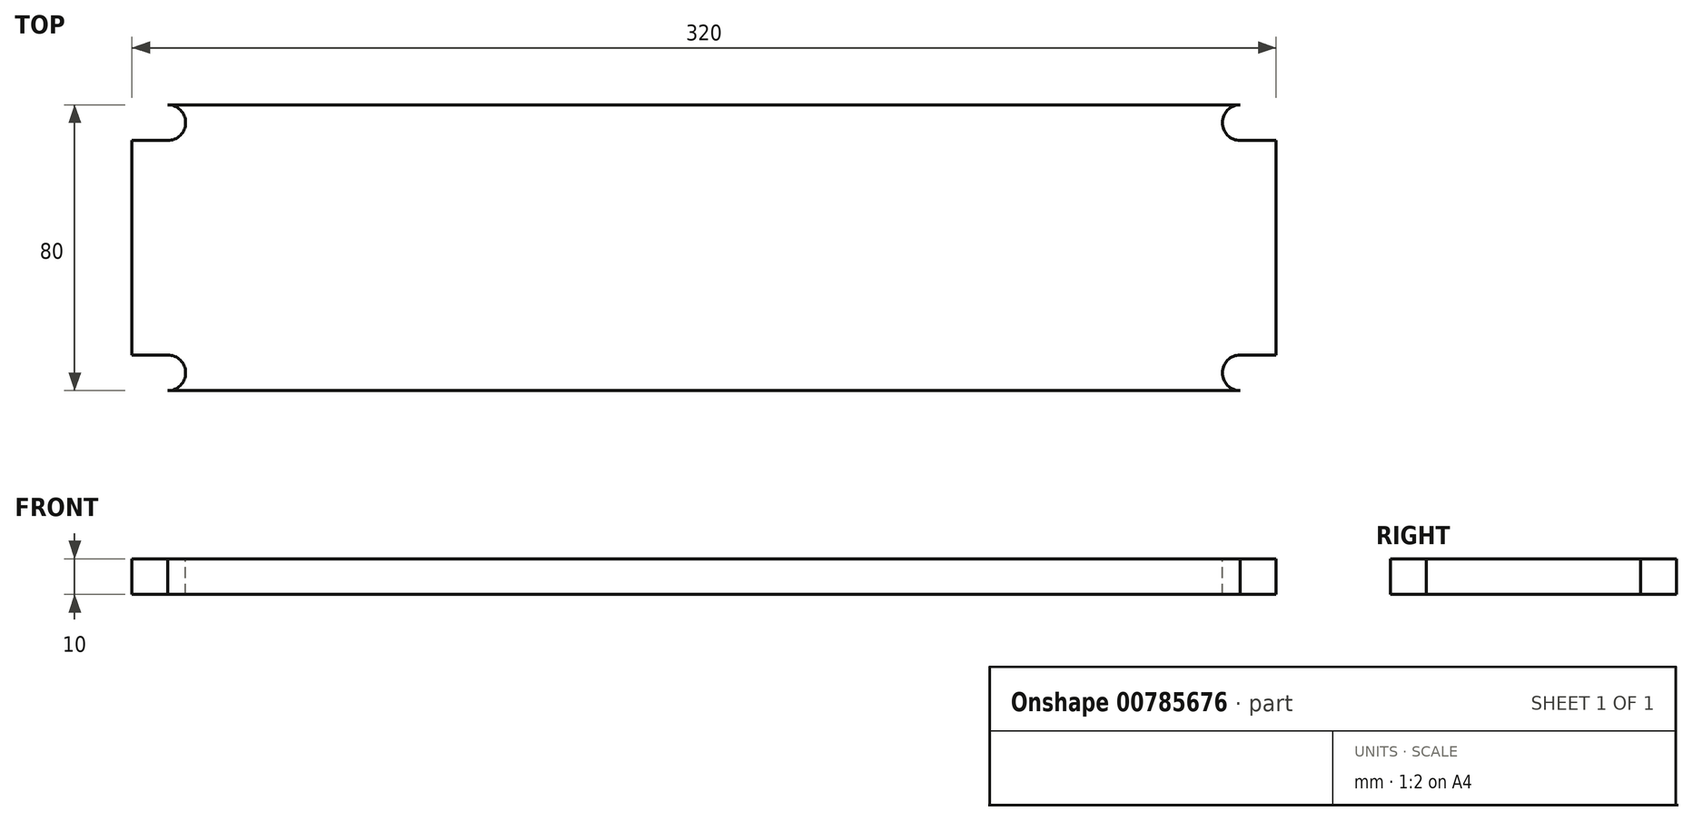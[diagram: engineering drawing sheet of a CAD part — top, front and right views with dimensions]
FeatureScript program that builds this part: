
annotation { "Feature Type Name" : "Feature", "Feature Type Description" : "" }
export const myFeature = defineFeature(function(context is Context, id is Id, definition is map)
    precondition{}
    {
        {
            assignVariable(context, id + "F0", {"name" : "plywood", "anyValue" : 10});
        }
        {
            var Q0;
            Q0=qCreatedBy(makeId("Top.planeOp"),FACE);
            var sketch = newSketch(context, id + "F1", { "sketchPlane" : qUnion([Q0])});
            skLineSegment(sketch, "E0.bottom", {"start": v(150, -40) * mm, "end": v(-150, -40) * mm});
            skLineSegment(sketch, "E0.top", {"start": v(150, 40) * mm, "end": v(-150, 40) * mm});
            skLineSegment(sketch, "E0.left", {"start": v(150, -40) * mm, "end": v(150, -30) * mm});
            skLineSegment(sketch, "E0.right", {"start": v(-150, -40) * mm, "end": v(-150, -30) * mm});
            skPoint(sketch, "E0.middle", {"position": v(0, 0) * mm});
            skLineSegment(sketch, "E1", {"start": v(-150, 0) * mm, "end": v(150, 0) * mm, "construction": true});
            skLineSegment(sketch, "E2.bottom", {"start": v(-160, 30) * mm, "end": v(-150, 30) * mm});
            skLineSegment(sketch, "E2.top", {"start": v(-160, -30) * mm, "end": v(-150, -30) * mm});
            skLineSegment(sketch, "E2.left", {"start": v(-160, 30) * mm, "end": v(-160, -30) * mm});
            skPoint(sketch, "E2.middle", {"position": v(-150, 0) * mm});
            skLineSegment(sketch, "E3.bottom", {"start": v(160, 30) * mm, "end": v(150, 30) * mm});
            skLineSegment(sketch, "E3.top", {"start": v(160, -30) * mm, "end": v(150, -30) * mm});
            skLineSegment(sketch, "E3.left", {"start": v(160, 30) * mm, "end": v(160, -30) * mm});
            skPoint(sketch, "E3.middle", {"position": v(150, 0) * mm});
            skLineSegment(sketch, "E4.trimOffspring", {"start": v(-150, 30) * mm, "end": v(-150, 40) * mm});
            skPoint(sketch, "E5.orphan", {"position": v(-140, 30) * mm});
            skPoint(sketch, "E2.right.end.orphan", {"position": v(-140, -30) * mm});
            skLineSegment(sketch, "E6.trimOffspring", {"start": v(150, 30) * mm, "end": v(150, 40) * mm});
            skPoint(sketch, "E7.orphan", {"position": v(140, -30) * mm});
            skPoint(sketch, "E8.orphan", {"position": v(140, 30) * mm});
            skSolve(sketch);
        }
        {
            var Q0;
            Q0=makeQuery(id+"F1.imprint","IMPRINT",FACE,{"disambiguationData":[TD([[makeQuery(id+"F1.imprint","IMPRINT",EDGE,{"derivedFrom":sQuery(id+"F1.wireOp",EDGE,"E0.bottom")}),-1.0]])]});
            extrude(context, id + "F2", {"entities" : qUnion([Q0]), "depth" : (getVariable(context, 'plywood')) * mm, "offsetDistance" : 25 * mm});
        }
        {
            var Q0;
            Q0=makeQuery(id+"F2.opExtrude","CAP_FACE",FACE,{"disambiguationData":[OSD([sQuery(id+"F1.wireOp",EDGE,"E0.bottom"),sQuery(id+"F1.wireOp",EDGE,"E0.top"),sQuery(id+"F1.wireOp",EDGE,"E0.left"),sQuery(id+"F1.wireOp",EDGE,"E0.right"),sQuery(id+"F1.wireOp",EDGE,"E2.bottom"),sQuery(id+"F1.wireOp",EDGE,"E2.top"),sQuery(id+"F1.wireOp",EDGE,"E2.left"),sQuery(id+"F1.wireOp",EDGE,"E3.bottom"),sQuery(id+"F1.wireOp",EDGE,"E3.top"),sQuery(id+"F1.wireOp",EDGE,"E3.left"),sQuery(id+"F1.wireOp",EDGE,"E4.trimOffspring"),sQuery(id+"F1.wireOp",EDGE,"E6.trimOffspring")])],"isStart":false});
            var sketch = newSketch(context, id + "F3", { "sketchPlane" : qUnion([Q0])});
            skArc(sketch, "E9", {"start": v(-150, 30) * mm, "mid": v(-145, 35) * mm, "end": v(-150, 40) * mm});
            skArc(sketch, "E10", {"start": v(-150, -40) * mm, "mid": v(-145, -35) * mm, "end": v(-150, -30) * mm});
            skArc(sketch, "E11", {"start": v(150, 40) * mm, "mid": v(145, 35) * mm, "end": v(150, 30) * mm});
            skArc(sketch, "E12", {"start": v(150, -30) * mm, "mid": v(145, -35) * mm, "end": v(150, -40) * mm});
            skSolve(sketch);
        }
        {
            var Q0;
            {var subQ0=sQuery(id+"F3.wireOp",EDGE,"E10");Q0=makeQuery(id+"F3.imprint","IMPRINT",FACE,{"disambiguationData":[TD([[makeQuery(id+"F3.imprint","IMPRINT",EDGE,{"derivedFrom":subQ0}),1.0]])]});}
            var Q1;
            {var subQ0=sQuery(id+"F3.wireOp",EDGE,"E9");Q1=makeQuery(id+"F3.imprint","IMPRINT",FACE,{"disambiguationData":[TD([[makeQuery(id+"F3.imprint","IMPRINT",EDGE,{"derivedFrom":subQ0}),1.0]])]});}
            var Q2;
            {var subQ0=sQuery(id+"F3.wireOp",EDGE,"E11");Q2=makeQuery(id+"F3.imprint","IMPRINT",FACE,{"disambiguationData":[TD([[makeQuery(id+"F3.imprint","IMPRINT",EDGE,{"derivedFrom":subQ0}),1.0]])]});}
            var Q3;
            {var subQ0=sQuery(id+"F3.wireOp",EDGE,"E12");Q3=makeQuery(id+"F3.imprint","IMPRINT",FACE,{"disambiguationData":[TD([[makeQuery(id+"F3.imprint","IMPRINT",EDGE,{"derivedFrom":subQ0}),1.0]])]});}
            extrude(context, id + "F4", {"entities" : qUnion([Q0, Q1, Q2, Q3]), "operationType" : NewBodyOperationType.REMOVE, "endBound" : BoundingType.THROUGH_ALL, "oppositeDirection" : true, "depth" : 25 * mm, "offsetDistance" : 25 * mm});
        }
    });
